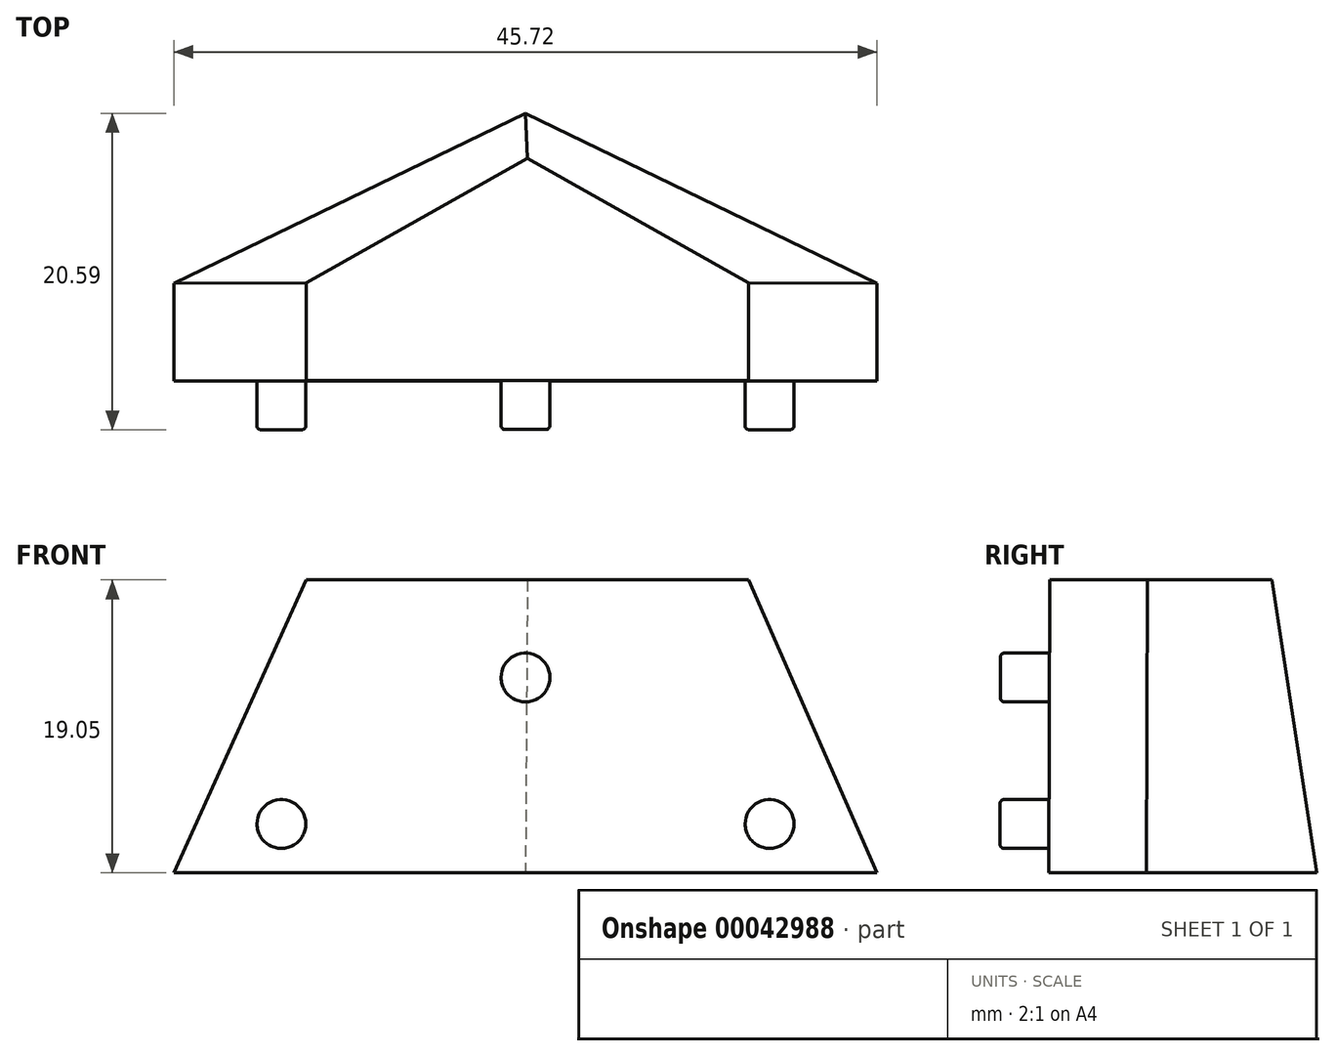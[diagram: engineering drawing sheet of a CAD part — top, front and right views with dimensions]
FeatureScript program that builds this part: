
annotation { "Feature Type Name" : "Feature", "Feature Type Description" : "" }
export const myFeature = defineFeature(function(context is Context, id is Id, definition is map)
    precondition{}
    {
        {
            var Q0;
            Q0=qCreatedBy(makeId("Top.planeOp"),FACE);
            var sketch = newSketch(context, id + "F0", { "sketchPlane" : qUnion([Q0])});
            skLineSegment(sketch, "E0", {"start": v(-55.93, -26.66) * mm, "end": v(-10.2, -26.66) * mm});
            skLineSegment(sketch, "E1", {"start": v(-10.2, -26.66) * mm, "end": v(-10.2, -20.3) * mm});
            skLineSegment(sketch, "E2", {"start": v(-55.93, -26.66) * mm, "end": v(-55.93, -20.3) * mm});
            skLineSegment(sketch, "E3", {"start": v(-33.07, -9.24) * mm, "end": v(-55.93, -20.3) * mm});
            skLineSegment(sketch, "E4", {"start": v(-33.07, -9.24) * mm, "end": v(-10.2, -20.3) * mm});
            skSolve(sketch);
        }
        {
            var Q0;
            Q0=makeQuery(id+"F0.imprint","IMPRINT",FACE,{"disambiguationData":[TD([[makeQuery(id+"F0.imprint","IMPRINT",EDGE,{"derivedFrom":sQuery(id+"F0.wireOp",EDGE,"E0")}),1.0]])]});
            cPlane(context, id + "F1", {"entities" : qUnion([Q0]), "cplaneType" : CPlaneType.OFFSET, "offset" : 19.05 * mm, "width" : 152.4 * mm, "height" : 152.4 * mm});
        }
        {
            var Q0;
            Q0=qCreatedBy(id+"F1.planeOp",FACE);
            var sketch = newSketch(context, id + "F2", { "sketchPlane" : qUnion([Q0])});
            skLineSegment(sketch, "E5", {"start": v(-47.33, -26.6) * mm, "end": v(-18.55, -26.6) * mm});
            skLineSegment(sketch, "E6", {"start": v(-18.55, -26.6) * mm, "end": v(-18.55, -20.25) * mm});
            skLineSegment(sketch, "E7", {"start": v(-18.55, -20.25) * mm, "end": v(-32.94, -12.16) * mm});
            skLineSegment(sketch, "E8", {"start": v(-47.33, -26.6) * mm, "end": v(-47.33, -20.25) * mm});
            skLineSegment(sketch, "E9", {"start": v(-47.33, -20.25) * mm, "end": v(-32.94, -12.16) * mm});
            skSolve(sketch);
        }
        {
            var Q0;
            Q0=makeQuery(id+"F2.imprint","IMPRINT",FACE,{"disambiguationData":[TD([[makeQuery(id+"F2.imprint","IMPRINT",EDGE,{"derivedFrom":sQuery(id+"F2.wireOp",EDGE,"E5")}),1.0]])]});
            var Q1;
            Q1=makeQuery(id+"F0.imprint","IMPRINT",FACE,{"disambiguationData":[TD([[makeQuery(id+"F0.imprint","IMPRINT",EDGE,{"derivedFrom":sQuery(id+"F0.wireOp",EDGE,"E0")}),1.0]])]});
            loft(context, id + "F3", {"sheetProfilesArray" : [{ "sheetProfileEntities" : qUnion([Q0]) }, { "sheetProfileEntities" : qUnion([Q1]) }]});
        }
        {
            var Q0;
            Q0=makeQuery(id+"F3.opLoft","SWEPT_FACE",FACE,{"disambiguationData":[OSD([sQuery(id+"F0.wireOp",EDGE,"E0"),sQuery(id+"F0.wireOp",EDGE,"E1"),sQuery(id+"F0.wireOp",EDGE,"E2"),sQuery(id+"F2.wireOp",EDGE,"E5"),sQuery(id+"F2.wireOp",EDGE,"E6"),sQuery(id+"F2.wireOp",EDGE,"E8")])]});
            var sketch = newSketch(context, id + "F4", { "sketchPlane" : qUnion([Q0])});
            skCircle(sketch, "E10", {"center": v(-48.94, 3.1) * mm, "radius": 1.59 * mm});
            skCircle(sketch, "E11", {"center": v(-17.2, 3.1) * mm, "radius": 1.59 * mm});
            skCircle(sketch, "E12", {"center": v(-33.07, 12.62) * mm, "radius": 1.59 * mm});
            skSolve(sketch);
        }
        {
            var Q0;
            Q0=makeQuery(id+"F4.imprint","IMPRINT",FACE,{"disambiguationData":[TD([[makeQuery(id+"F4.imprint","IMPRINT",EDGE,{"derivedFrom":sQuery(id+"F4.wireOp",EDGE,"E10")}),1.0]])]});
            var Q1;
            Q1=makeQuery(id+"F4.imprint","IMPRINT",FACE,{"disambiguationData":[TD([[makeQuery(id+"F4.imprint","IMPRINT",EDGE,{"derivedFrom":sQuery(id+"F4.wireOp",EDGE,"E12")}),1.0]])]});
            var Q2;
            Q2=makeQuery(id+"F4.imprint","IMPRINT",FACE,{"disambiguationData":[TD([[makeQuery(id+"F4.imprint","IMPRINT",EDGE,{"derivedFrom":sQuery(id+"F4.wireOp",EDGE,"E11")}),1.0]])]});
            extrude(context, id + "F5", {"entities" : qUnion([Q0, Q1, Q2]), "operationType" : NewBodyOperationType.ADD, "depth" : 3.17 * mm});
        }
        {
            var Q0;
            Q0=makeQuery(id+"F5.opExtrude","CAP_EDGE",EDGE,{"disambiguationData":[OSD([sQuery(id+"F4.wireOp",EDGE,"E10")])],"isStart":false});
            var Q1;
            Q1=makeQuery(id+"F5.opExtrude","CAP_EDGE",EDGE,{"disambiguationData":[OSD([sQuery(id+"F4.wireOp",EDGE,"E12")])],"isStart":false});
            var Q2;
            Q2=makeQuery(id+"F5.opExtrude","CAP_EDGE",EDGE,{"disambiguationData":[OSD([sQuery(id+"F4.wireOp",EDGE,"E11")])],"isStart":false});
            fillet(context, id + "F6", {"entities" : qUnion([Q0, Q1, Q2]), "radius" : 0.25 * mm, "tangentPropagation" : true, "allowEdgeOverflow" : false});
        }
    });
